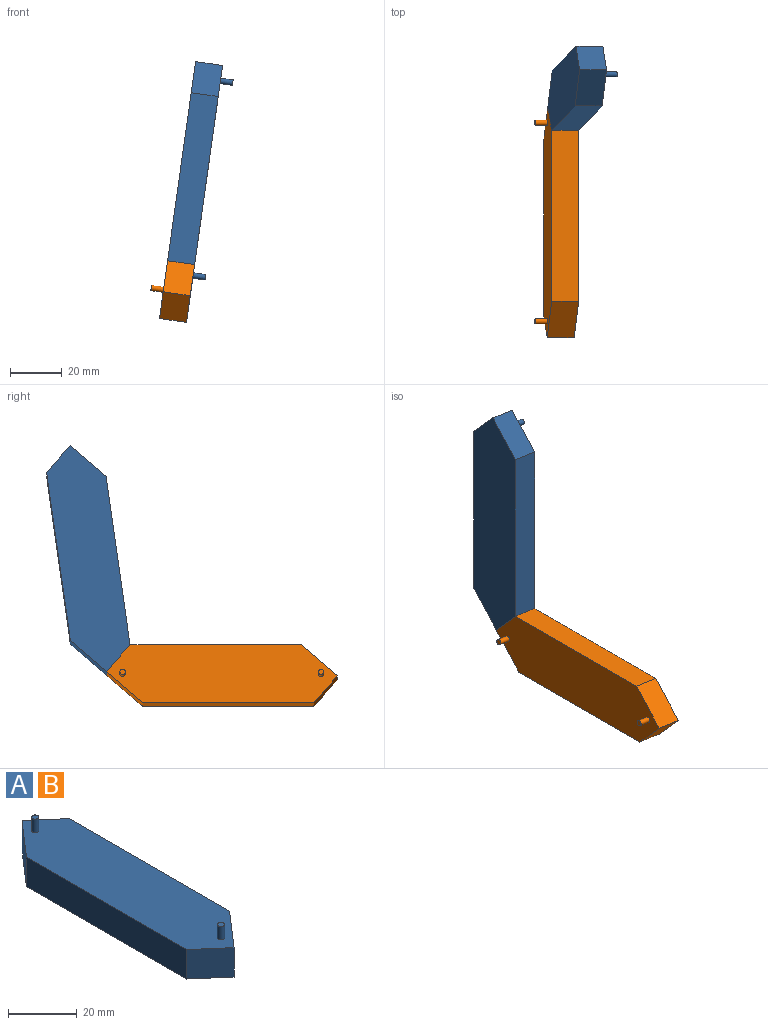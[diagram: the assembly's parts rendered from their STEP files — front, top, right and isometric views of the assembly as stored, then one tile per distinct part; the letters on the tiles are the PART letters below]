
ASSEMBLY  parts=2 mates=1
PART A: 12 faces, bbox 22.5x89x15.3 mm
  f0: plane 13.92x12.1mm, normal (-0.75,0.66,0), area 193.7mm2, adj f1,f5,f6,f7
  f1: plane 10.5x10.4mm, normal (0.66,0.75,0), area 144.7mm2, adj f0,f2,f6,f7
  f2: plane 66.04x10.5mm, normal (1,0,0), area 693.4mm2, adj f1,f3,f6,f7
  f3: plane 13.92x12.1mm, normal (0.75,-0.66,0), area 193.7mm2, adj f2,f4,f6,f7
  f4: plane 10.5x10.4mm, normal (-0.66,-0.75,0), area 144.7mm2, adj f3,f5,f6,f7
  f5: plane 66.04x10.5mm, normal (-1,0,0), area 693.4mm2, adj f0,f4,f6,f7
  f6: plane 89x22.5mm, normal (0,0,-1), area 1740.1mm2, adj f0,f1,f2,f3,f4,f5
  f7: plane 89x22.5mm, normal (0,0,1), area 1733.1mm2, adj f0,f1,f2,f3,f4,f5,f8,f10
  f8: cylinder r=1.05mm len=4.8mm, axis (0,0,-1), area 31.7mm2, adj f7,f9
  f9: plane 2.1x2.1mm, normal (0,0,1), area 3.5mm2, adj f8
  f10: cylinder r=1.05mm len=4.8mm, axis (0,0,-1), area 31.7mm2, adj f7,f11
  f11: plane 2.1x2.1mm, normal (0,0,1), area 3.5mm2, adj f10
PART B: same geometry as A
PLACE A rot(axis=(-0.63,0.55,-0.55),129deg) t=(87.84,8.82,150.92)mm
PLACE B rot(axis=(0.66,0,-0.75),180deg) t=(65.21,-5.25,65.34)mm
MATE fastened B.f4 <-> A.f1  axis (0.09,0.75,0.65) through (71.13,-9.77,69.76)mm
